# Revit family: RockPanel_Cladding
name_source: partatom
category: Generic Models
revit_build: Autodesk Revit 2017 (Build: 20171027_0315(x64)
units: mm (PartAtom-declared; Revit-internal decimal feet)

## family parameters
Can host rebar = No
Cut with Voids When Loaded = No
Host = Face
Part Type = Normal
Room Calculation Point = No
Round Connector Dimension = Use Diameter
Shared = No

## types (23) — shared parameters
Design country = Germany
Edition number = 1
Manufacture country = Germany
Manufacturer = RockPanel GmbH
Model = RockPanel Cladding
Product data URL = http://rockpanel.bimobject.com
Product family = FACADE ENGINEERING
Product group = Fasade Elements
zero-valued in all types: Default Elevation, Index

## per-type parameters (varying)
| type | Depth | Maximum Height | Maximum Width |
| RockPanel Colors - Durable - 6mm | 6 mm  [stored 0.019685 ft] | 1250 mm  [stored 4.10105 ft] | 2500 mm  [stored 8.2021 ft] |
| RockPanel Colors - Durable - 8mm | 8 mm  [stored 0.0262467 ft] | 1250 mm  [stored 4.10105 ft] | 2500 mm  [stored 8.2021 ft] |
| RockPanel Colors - Xtreme  - 8mm | 8 mm  [stored 0.0262467 ft] | 1250 mm  [stored 4.10105 ft] | 3050 mm  [stored 10.0066 ft] |
| RockPanel Colors - A2 - 9mm | 9 mm  [stored 0.0295276 ft] | 1200 mm | 3050 mm  [stored 10.0066 ft] |
| RockPanel Colors - Premium A2 - 11mm | 11 mm  [stored 0.0360892 ft] | 1200 mm | 3050 mm  [stored 10.0066 ft] |
| RockPanel Wood - Durable - 8mm | 8 mm  [stored 0.0262467 ft] | 1250 mm  [stored 4.10105 ft] | 3050 mm  [stored 10.0066 ft] |
| RockPanel Wood - Xtreme  - 8mm | 8 mm  [stored 0.0262467 ft] | 1250 mm  [stored 4.10105 ft] | 3050 mm  [stored 10.0066 ft] |
| RockPanel Wood - A2 - 9mm | 9 mm  [stored 0.0295276 ft] | 1250 mm  [stored 4.10105 ft] | 3050 mm  [stored 10.0066 ft] |
| RockPanel Wood - Premium A2 - 11mm | 11 mm  [stored 0.0360892 ft] | 1250 mm  [stored 4.10105 ft] | 3050 mm  [stored 10.0066 ft] |
| RockPanel Metalics - Durable - 8mm | 8 mm  [stored 0.0262467 ft] | 1200 mm | 2500 mm  [stored 8.2021 ft] |
| RockPanel Metalics - Xtreme  - 8mm | 8 mm  [stored 0.0262467 ft] | 1200 mm | 3050 mm  [stored 10.0066 ft] |
| RockPanel Metalics - A2 - 9mm | 9 mm  [stored 0.0295276 ft] | 1200 mm | 3050 mm  [stored 10.0066 ft] |
| RockPanel Metalics - Premium A2 - 11mm | 11 mm  [stored 0.0360892 ft] | 1200 mm | 3050 mm  [stored 10.0066 ft] |
| RockPanel Natural - Durable - 8mm | 8 mm  [stored 0.0262467 ft] | 1250 mm  [stored 4.10105 ft] | 2500 mm  [stored 8.2021 ft] |
| RockPanel Natural - Durable - 10mm | 10 mm  [stored 0.0328084 ft] | 1250 mm  [stored 4.10105 ft] | 2500 mm  [stored 8.2021 ft] |
| RockPanel Natural - Xtreme  - 8mm | 8 mm  [stored 0.0262467 ft] | 1250 mm  [stored 4.10105 ft] | 3050 mm  [stored 10.0066 ft] |
| RockPanel Natural - Xtreme  - 10mm | 10 mm  [stored 0.0328084 ft] | 1250 mm  [stored 4.10105 ft] | 3050 mm  [stored 10.0066 ft] |
| RockPanel Ply - 6mm | 6 mm  [stored 0.019685 ft] | 1250 mm  [stored 4.10105 ft] | 3050 mm  [stored 10.0066 ft] |
| RockPanel Ply - 8mm | 8 mm  [stored 0.0262467 ft] | 1250 mm  [stored 4.10105 ft] | 3050 mm  [stored 10.0066 ft] |
| RockPanel Ply - 10mm | 10 mm  [stored 0.0328084 ft] | 1250 mm  [stored 4.10105 ft] | 3050 mm  [stored 10.0066 ft] |
| RockPanel Chameleon - Durable - 8mm | 8 mm  [stored 0.0262467 ft] | 1200 mm | 3050 mm  [stored 10.0066 ft] |
| RockPanel Chameleon - Xtreme  - 9mm | 9 mm  [stored 0.0295276 ft] | 1200 mm | 3050 mm  [stored 10.0066 ft] |
| RockPanel Chameleon - Premium A2  - 11mm | 11 mm  [stored 0.0360892 ft] | 1200 mm | 3050 mm  [stored 10.0066 ft] |

note: [stored X ft] marks values corroborated as IEEE doubles in the binary element streams (Revit-internal decimal feet)

## geometry (parser evidence)
native form markers: Blend x2, Sweep x5
no freeform markers — native parametric forms only
